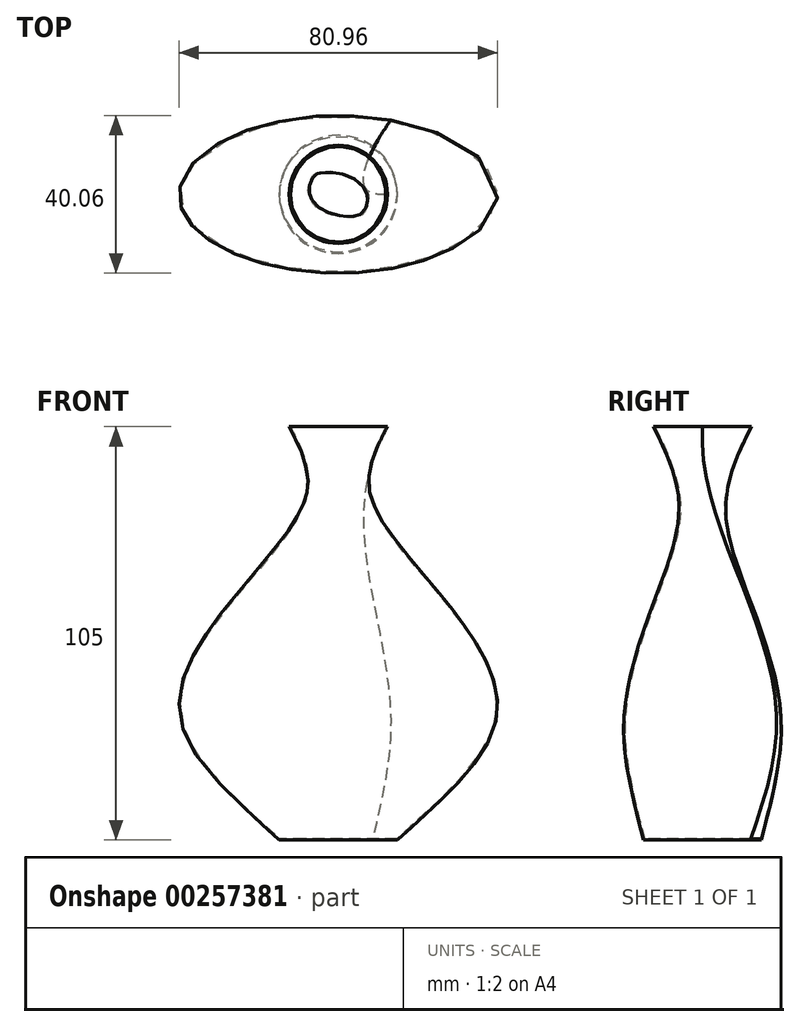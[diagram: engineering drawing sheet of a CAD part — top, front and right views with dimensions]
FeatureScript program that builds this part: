
annotation { "Feature Type Name" : "Feature", "Feature Type Description" : "" }
export const myFeature = defineFeature(function(context is Context, id is Id, definition is map)
    precondition{}
    {
        {
            var Q0;
            Q0=qCreatedBy(makeId("Top.planeOp"),FACE);
            var sketch = newSketch(context, id + "F0", { "sketchPlane" : qUnion([Q0])});
            skCircle(sketch, "E0", {"center": v(0, 0) * mm, "radius": 12.5 * mm});
            skSolve(sketch);
        }
        {
            var Q0;
            Q0=qCreatedBy(makeId("Top.planeOp"),FACE);
            cPlane(context, id + "F1", {"entities" : qUnion([Q0]), "cplaneType" : CPlaneType.OFFSET, "offset" : 5 * mm, "oppositeDirection" : true, "width" : 150 * mm, "height" : 150 * mm});
        }
        {
            var Q0;
            Q0=qCreatedBy(id+"F1.planeOp",FACE);
            var sketch = newSketch(context, id + "F2", { "sketchPlane" : qUnion([Q0])});
            skCircle(sketch, "E1", {"center": v(0, 0) * mm, "radius": 10 * mm});
            skSolve(sketch);
        }
        {
            var Q0;
            Q0=qCreatedBy(id+"F1.planeOp",FACE);
            cPlane(context, id + "F3", {"entities" : qUnion([Q0]), "cplaneType" : CPlaneType.OFFSET, "offset" : 70 * mm, "oppositeDirection" : true, "width" : 150 * mm, "height" : 150 * mm});
        }
        {
            var Q0;
            Q0=qCreatedBy(id+"F3.planeOp",FACE);
            var sketch = newSketch(context, id + "F4", { "sketchPlane" : qUnion([Q0])});
            skEllipse(sketch, "E2", {"center": v(0, 0) * mm, "majorRadius": 20 * mm, "minorRadius": 40 * mm, "majorAxis": v(0, 1)});
            skSolve(sketch);
        }
        {
            var Q0;
            Q0=qCreatedBy(id+"F3.planeOp",FACE);
            cPlane(context, id + "F5", {"entities" : qUnion([Q0]), "cplaneType" : CPlaneType.OFFSET, "offset" : 30 * mm, "oppositeDirection" : true, "width" : 150 * mm, "height" : 150 * mm});
        }
        {
            var Q0;
            Q0=qCreatedBy(id+"F5.planeOp",FACE);
            var sketch = newSketch(context, id + "F6", { "sketchPlane" : qUnion([Q0])});
            skCircle(sketch, "E3", {"center": v(0, 0) * mm, "radius": 15 * mm});
            skSolve(sketch);
        }
        {
            var Q0;
            Q0=makeQuery(id+"F0.imprint","IMPRINT",FACE,{"disambiguationData":[TD([[makeQuery(id+"F0.imprint","IMPRINT",EDGE,{"derivedFrom":sQuery(id+"F0.wireOp",EDGE,"E0")}),1.0]])]});
            var Q1;
            Q1=makeQuery(id+"F2.imprint","IMPRINT",FACE,{"disambiguationData":[TD([[makeQuery(id+"F2.imprint","IMPRINT",EDGE,{"derivedFrom":sQuery(id+"F2.wireOp",EDGE,"E1")}),1.0]])]});
            var Q2;
            Q2=makeQuery(id+"F4.imprint","IMPRINT",FACE,{"disambiguationData":[TD([[makeQuery(id+"F4.imprint","IMPRINT",EDGE,{"derivedFrom":sQuery(id+"F4.wireOp",EDGE,"E2")}),1.0]])]});
            var Q3;
            Q3=makeQuery(id+"F6.imprint","IMPRINT",FACE,{"disambiguationData":[TD([[makeQuery(id+"F6.imprint","IMPRINT",EDGE,{"derivedFrom":sQuery(id+"F6.wireOp",EDGE,"E3")}),1.0]])]});
            loft(context, id + "F7", {"sheetProfilesArray" : [{ "sheetProfileEntities" : qUnion([Q0]) }, { "sheetProfileEntities" : qUnion([Q1]) }, { "sheetProfileEntities" : qUnion([Q2]) }, { "sheetProfileEntities" : qUnion([Q3]) }]});
        }
        {
            var Q0;
            Q0=makeQuery(id+"F7.opLoft","CAP_FACE",FACE,{"disambiguationData":[OSD([makeQuery(id+"F0.imprint","IMPRINT",FACE,{"disambiguationData":[TD([[makeQuery(id+"F0.imprint","IMPRINT",EDGE,{"derivedFrom":sQuery(id+"F0.wireOp",EDGE,"E0")}),1.0]])]})])],"isStart":true});
            shell(context, id + "F8", {"entities" : qUnion([Q0]), "thickness" : 0.3 * mm});
        }
    });
